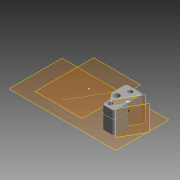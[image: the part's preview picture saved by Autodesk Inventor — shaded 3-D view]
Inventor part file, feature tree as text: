
AUTODESK INVENTOR PART (.ipt)
format: ipt  version: 2015 (Build 190159000, 159)  size: 123,904 bytes
history: native  units: mm
features: plane x5, reference x4, sketch x3, extrude x1, hole x1, fillet x1, projected_geometry x1
ambient origin geometry x8: Origin, YZ Plane, XZ Plane, XY Plane, X Axis, Y Axis, Z Axis, Center Point
bodies: Solid1 (feature_tree)
feature tree (16):
  plane  "Work Plane1"
  plane  "Work Plane2"
  sketch  "Sketch1"  dims[d1=3.0mm d2=10.0mm d3=0.0mm]
  extrude  "Extrusion1"  Depth=10.0mm TaperAngle=0.0deg
  plane  "Work Plane4"
  sketch  "Sketch4"  dims[d6=4.0mm d16=10.0mm]
  plane  "Work Plane8"
  hole  "Hole2"  [1 undecoded]
  fillet  "Fillet1"  Radius=2.0mm
  reference  "Reference3"
  reference  "Reference4"
  reference  "Reference11"
  projected_geometry  "Projected Loop1"
  reference  "Reference12"
  plane  "Work Plane7"
  sketch  "Sketch7"  dims[d17=2.459mm d18=6.0mm d19=4.0mm d20=2.0mm d21=90.0deg d22=8.0mm d23=20.594885mm d24=2.0mm d26=26.0mm d29=7.0mm]
note: 1 required parameter value undecoded (feature->parameter linkage not recoverable at this tier; creation-order binding heuristic only, values carry confidence <= 0.55)
